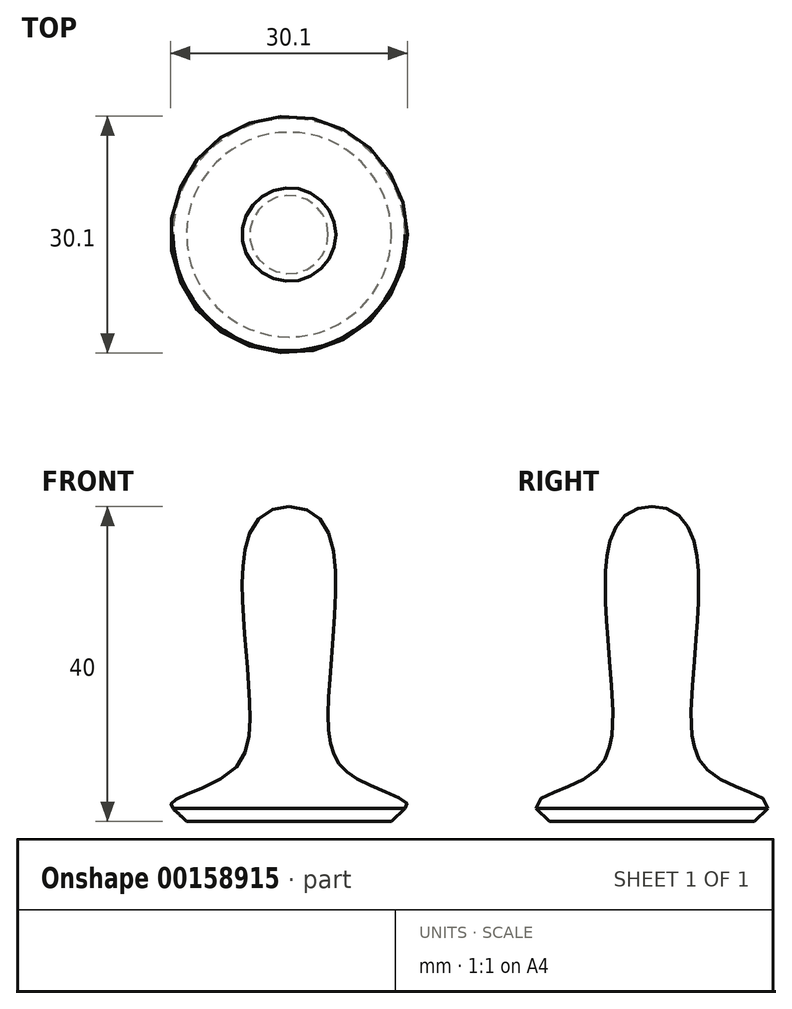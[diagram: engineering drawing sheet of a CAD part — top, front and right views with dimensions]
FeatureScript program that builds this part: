
annotation { "Feature Type Name" : "Feature", "Feature Type Description" : "" }
export const myFeature = defineFeature(function(context is Context, id is Id, definition is map)
    precondition{}
    {
        {
            var Q0;
            Q0=qCreatedBy(makeId("Front.planeOp"),FACE);
            var sketch = newSketch(context, id + "F0", { "sketchPlane" : qUnion([Q0])});
            skLineSegment(sketch, "E0", {"start": v(13, 0) * mm, "end": v(0, 0) * mm});
            skLineSegment(sketch, "E1", {"start": v(0, 0) * mm, "end": v(0, 40) * mm});
            skFitSpline(sketch, "E2", {"points": [v(0, 40) * mm, v(5.85, 26.9) * mm, v(5.3, 9.78) * mm, v(9.78, 4.81) * mm, v(14.74, 1.64) * mm], "startDerivative": vector(60.84, 0.08) * mm, "endDerivative": vector(-22.79, -13.59) * mm});
            skLineSegment(sketch, "E3", {"start": v(13, 0) * mm, "end": v(14.74, 1.64) * mm});
            skSolve(sketch);
        }
        {
            var Q0;
            Q0=makeQuery(id+"F0.imprint","IMPRINT",FACE,{"disambiguationData":[TD([[makeQuery(id+"F0.imprint","IMPRINT",EDGE,{"derivedFrom":sQuery(id+"F0.wireOp",EDGE,"E0")}),-1.0]])]});
            var Q1;
            Q1=sQuery(id+"F0.wireOp",EDGE,"E1");
            revolve(context, id + "F1", {"entities" : qUnion([Q0]), "axis" : qUnion([Q1]), "revolveType" : RevolveType.FULL});
        }
    });
